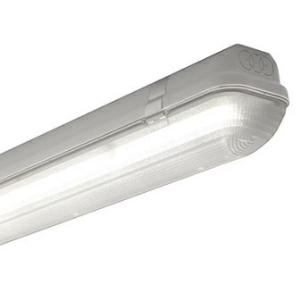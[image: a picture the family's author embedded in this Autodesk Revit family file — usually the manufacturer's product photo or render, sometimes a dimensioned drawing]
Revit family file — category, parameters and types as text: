
# Revit family: 3f_filippi_-_3f_linda_atex_3f_filippi_-_58474_-_3f_linda_led_1x30w_atex_3d_l1570
name_source: partatom
category: Lighting Fixtures
units: mm (PartAtom-declared; Revit-internal decimal feet)

## family parameters
Cut with Voids When Loaded = No
Host = Face
Light Source = No
Part Type = Normal
Room Calculation Point = No
Round Connector Dimension = Use Diameter
Shared = No

## types (1)
- 3F Filippi - 3F Linda ATEX (1 x LED, 5180 lm, 33.5 W, 4000 K)
    Apparent Load = 34 VA
    Approval mark = ENEC
    CIE Flux Codes = 44 77 94 97 100
    Color Rendering = 80
    Color Temperature = 4000 K
    Control Gear = Electronic ballast
    Default Elevation = 1800 mm
    Description = ILLUMINOTECHNICAL
Luminous efficiency 100% (DLOR 97%, ULOR 3%).
Initial luminous flux of the luminaire 5180 lm.
Controlled symmetric distribution.
Installation Interdistance Transv.D = 1.77 x hu - Long.D = 1.17 x hu.
Tabular UGR (CIE 117 - 4H-8H; S=0.25H; 70/50/20): RUG 22.1 - 23.1.
Beam angle: 109° - 64°.
Luminous efficacy 155 lm/W.
Lifetime (L93/B10): 30000 h. (tq+25°C)
Lifetime (L90/B10): 50000 h. (tq+25°C)
Lifetime (L85/B10): 80000 h. (tq+25°C)
Lifetime (L80/B10): 100000 h. (tq+25°C)
Lifetime (L85/B10): 50000 h. (tq+35°C)
Sudden decreased luminous flux after 50000 hours: 0% (C0).
Photobiological safety in compliance with IEC/TR 62778: RG0 risk exempt, (IEC 62471).
In compliance with IEC/EN 62722-2-1 - IEC/EN 62717 standards.

SOURCE
Linear LED module 30W/840.
Energy efficiency class (UE 2019/2020 - UE 2019/2015): D.
CIE 13.3 Colour rendering index: CRI >80 (R9 <50%).
IES TM-30 Fidelity Index: Rf = 84 Rg = 95.
CCT nominal colour temperature 4000 K.
Colour initial tolerance (MacAdam): SDCM 3.

MECHANICAL
Self-extinguishing V2 polycarbonate housing, injection moulded, RAL 7035 grey.
Ecologic anti-aging injected sealing gasket.
Diffuser in self-extinguishing V2 polycarbonate, photo-engraved interior, UV stabilised, injection moulded with smooth outer surface, tamper-proof opening.
Gear-holder reflector in hot-dip galvanised steel, painted with white polyester base.
Snug fit safety snap-lock clips for diffuser mounting in stainless steel, screwdriver opening.
Fixing brackets in stainless steel.
Possibility for technicians to access the interior of the luminaire.
Luminaire with limited surface temperature. - D - (EN 60598-2-24)
Dimensions: 1570x100 mm, height 100 mm. Weight 2.447 kg.
IP66 protection degree.
Mechanical strength to impacts IK10 (20 joule).
Glow-wire test resistance 850°C.

ELECTRICAL
Halogen Free electronic wiring 230V-50/60Hz, power factor 0.95, THD <25%, constant output current, SELV, class I, 1 driver.
Power of the luminaire 33.5 W.
CE - IEC 60598-1 - EN 60598-1.
SAFE FLICKER: PstLM=<1 and SVM=<0.4 (IEC TR 61547-1 and IEC TR 63158), to ensure a more comfortable and safe light.
Luminaire compliant with EN 60598-2-22 for power supply from a centralised emergency system CPSS (Central Power Supply System), not incorporated in the luminaire - high risk areas excluded. The default power and flux are 100% in AC and 100% in DC.
Ambient temperature from -20°C to +35°C.
Temperature class T6 max 85°C.
Entry for power-supply cable through ATEX M20x1,5mm polyamide cable gland, supplied.
Relative humidity UR: <85%.

INSTALLATION
Ceiling / Suspended / Wall.
All accessories dedicated to this product are available on the Catalog and on our website www.3F-Filippi.com.

APPLICATIONS
Environments with ATEX explosive atmosphere (Conformity 2014/34/UE, EN IEC 60079-0, EN 60079-31): Group II, Category 3D (Ex Tc IIIC T85°C Dc).
Suitable product for food production plants (HACCP), IFS (Food Version 6), BRC (GSFS Food Version 7).
Dry, dusty indoor environments, subject to occasional water splashes.
Virtually shatterproof polycarbonate compatibly with the fumes / atmospheres that compromise the elasticity of plastic materials.
Not suitable for installation on surfaces subject to important vibrations, exposed to weather conditions, on ropes or poles.
Suitable for illumination of public car parks and parking grounds referred to DIN 67528:2018-04.

WARNING
Fixture not suitable for cold stores with an ambient temperature <0°C and/or relative humidity >85%.
Luminaire designed for disposal/recycling at end-of-life.
Replaceable (LED only) light source by a professional. Replaceable control gear by a professional.
    Height = 100 mm  [stored 0.328084 ft]
    Lamp = 1 x LED
    Lamp Light Flux = 5180 lm
    Lamp Power = 33.5 W
    Lamp count = 1
    Length = 1570 mm
    Lifetime = 50000 h
    Luminous efficacy = 155 lm/W
    Manufacturer = 3F Filippi
    ModVariant = No
    Model = 3F Filippi - 58474 - 3F Linda LED 1x30W ATEX 3D L1570
    Mounting Place = Ceiling
    Mounting Type = Pendant
    Number of Poles = 1
    OnlyDefault = Yes
    Power Factor = 1
    Product Name = 3F Filippi - 3F Linda ATEX
    Product group = pendant luminaire
    ProductGroupID = 9
    Protection Class = Protection class I
    Protection Degree = IP 66
    RLX_Detail_Level = 1
    RLX_Emergency_Light_Flux = 0 lm
    RLX_Emergency_Type = 0
    RLX_Emergency_Type_DB = No
    RlxData = <blob elided: 69165 chars, md5=6b0b9229>
    Socket = socket
    Standby Power = 0 W
    System Light Flux = 5180 lm
    System Power = 34 W
    Type Comments = Product without accessories
    Type Image = 3ffilippi_3f_linda_led_1x.jpg
    URL = http://relux.com
    VarID = ---
    Voltage = 0 V
    Weight = 0.00 kg
    Width = 100 mm  [stored 0.328084 ft]

note: [stored X ft] marks values corroborated as IEEE doubles in the binary element streams (Revit-internal decimal feet)

## geometry (parser evidence)
native form markers: Blend x4, Sweep x9
no freeform markers — native parametric forms only
